# Revit family: QSC CXD-Q Amplifiers
name_source: partatom
category: Generic Models
revit_build: Autodesk Revit Architecture 2012 (Build: 20110309_2315(x64)
units: mm (PartAtom-declared; Revit-internal decimal feet)

## types (3) — shared parameters
Default Elevation = 0' - 0"
Height = 0' - 3 1/2"
Manufacturer = QSC Audio Products, LLC
Manufacturer URL = http://www.qscaudio.com
Product Documentation Link = http://qsc.com
Product Page URL = http://qsc.com
Regulatory Compliance = UL, CE, RoHS/WEEE, FCC Class A
URL = http://qsc.com
Voltage AC = 100-240 at 50-60 Hz
Width = 1' - 7"

## per-type parameters (varying)
| type | Depth | Description | Weight Dimensional (kg) | Weight Dimensional (lb) | Weight Product (kg) | Weight Product (lb) |
| CXD4.2Q | 1' - 0" | 2000 Watt Multi-Channel Network Processing Amplifier | 10 | 22 | 8.4 | 18.5 |
| CXD4.3Q | 1' - 4" | 3000 Watt Multi-Channel Network Processing Amplifier | 11.3 | 25 | 9.5 | 21 |
| CXD4.5Q | 1' - 4" | 5000 Watt Multi-Channel Network Processing Amplifier | 11.8 | 26 | 10 | 22 |

note: column(s) folded — value = type name in every type: Model

## geometry (parser evidence)
native form markers: Blend x1, Sweep x10
no freeform markers — native parametric forms only
